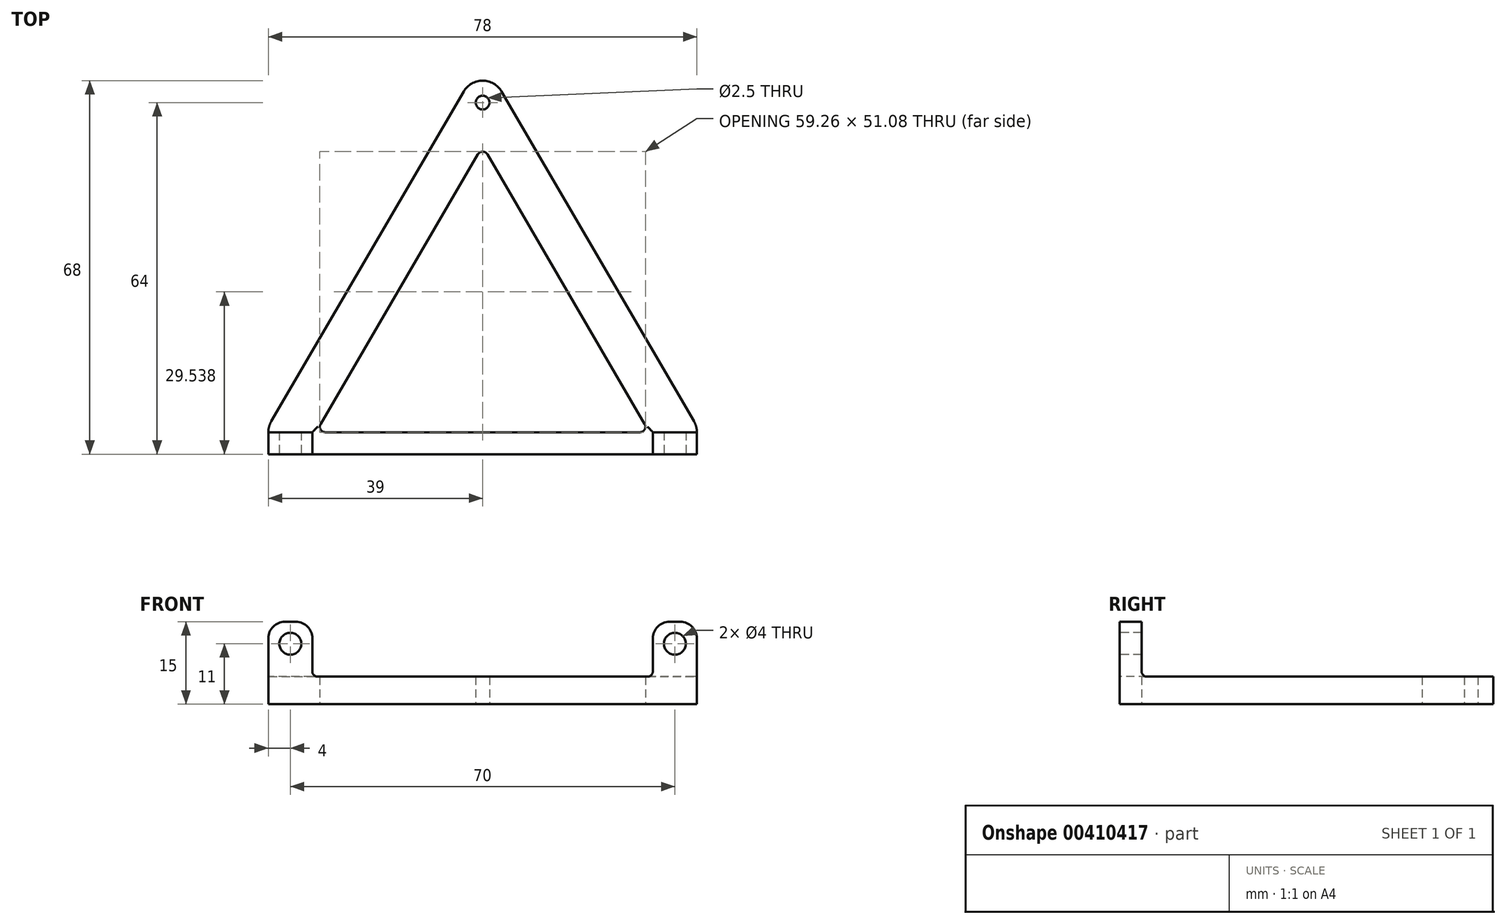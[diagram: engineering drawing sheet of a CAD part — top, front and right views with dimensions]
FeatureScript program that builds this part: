
annotation { "Feature Type Name" : "Feature", "Feature Type Description" : "" }
export const myFeature = defineFeature(function(context is Context, id is Id, definition is map)
    precondition{}
    {
        {
            var Q0;
            Q0=qCreatedBy(makeId("Top.planeOp"),FACE);
            var sketch = newSketch(context, id + "F0", { "sketchPlane" : qUnion([Q0])});
            skLineSegment(sketch, "E0", {"start": v(-35, 4) * mm, "end": v(35, 4) * mm, "construction": true});
            skLineSegment(sketch, "E1", {"start": v(35, 4) * mm, "end": v(0, 64) * mm, "construction": true});
            skLineSegment(sketch, "E2", {"start": v(0, 64) * mm, "end": v(-35, 4) * mm, "construction": true});
            skLineSegment(sketch, "E3.0", {"start": v(-3.46, 66.02) * mm, "end": v(-38.46, 6.02) * mm});
            skLineSegment(sketch, "E3.1", {"start": v(38.46, 6.02) * mm, "end": v(3.46, 66.02) * mm});
            skLineSegment(sketch, "E4.left", {"start": v(-39, 0) * mm, "end": v(-39, 4) * mm});
            skPoint(sketch, "E5", {"position": v(0, 4) * mm});
            skArc(sketch, "E6", {"start": v(-38.46, 6.02) * mm, "mid": v(-38.86, 5.04) * mm, "end": v(-39, 4) * mm});
            skLineSegment(sketch, "E7.0", {"start": v(-0.86, 54.58) * mm, "end": v(-29.5, 5.5) * mm});
            skLineSegment(sketch, "E7.1", {"start": v(29.5, 5.5) * mm, "end": v(0.86, 54.58) * mm});
            skLineSegment(sketch, "E8", {"start": v(-28.63, 4) * mm, "end": v(28.63, 4) * mm});
            skLineSegment(sketch, "E9", {"start": v(39, 4) * mm, "end": v(39, 0) * mm});
            skArc(sketch, "E10", {"start": v(38.46, 6.02) * mm, "mid": v(38.86, 5.04) * mm, "end": v(39, 4) * mm});
            skLineSegment(sketch, "E11", {"start": v(-39, 0) * mm, "end": v(39, 0) * mm});
            skPoint(sketch, "E12.visualSharp", {"position": v(0, 71.94) * mm});
            skArc(sketch, "E12.filletArc", {"start": v(3.46, 66.02) * mm, "mid": v(0, 68) * mm, "end": v(-3.46, 66.02) * mm});
            skPoint(sketch, "E13.visualSharp", {"position": v(0, 56.06) * mm});
            skArc(sketch, "E13.filletArc", {"start": v(0.86, 54.58) * mm, "mid": v(0, 55.08) * mm, "end": v(-0.86, 54.58) * mm});
            skPoint(sketch, "E14.visualSharp", {"position": v(-30.37, 4) * mm});
            skArc(sketch, "E14.filletArc", {"start": v(-29.5, 5.5) * mm, "mid": v(-29.5, 4.5) * mm, "end": v(-28.63, 4) * mm});
            skPoint(sketch, "E15.visualSharp", {"position": v(30.37, 4) * mm});
            skArc(sketch, "E15.filletArc", {"start": v(28.63, 4) * mm, "mid": v(29.5, 4.5) * mm, "end": v(29.5, 5.5) * mm});
            skCircle(sketch, "E16", {"center": v(0, 64) * mm, "radius": 1.25 * mm});
            skSolve(sketch);
        }
        {
            var Q0;
            Q0=makeQuery(id+"F0.imprint","IMPRINT",FACE,{"disambiguationData":[TD([[makeQuery(id+"F0.imprint","IMPRINT",EDGE,{"derivedFrom":sQuery(id+"F0.wireOp",EDGE,"E3.0")}),1.0]])]});
            extrude(context, id + "F1", {"entities" : qUnion([Q0]), "depth" : 5 * mm});
        }
        {
            var Q0;
            Q0=qCreatedBy(makeId("Front.planeOp"),FACE);
            var sketch = newSketch(context, id + "F2", { "sketchPlane" : qUnion([Q0])});
            skLineSegment(sketch, "E17.bottom", {"start": v(-39, 0) * mm, "end": v(-31, 0) * mm});
            skLineSegment(sketch, "E17.top", {"start": v(-36, 15) * mm, "end": v(-34, 15) * mm});
            skLineSegment(sketch, "E17.left", {"start": v(-39, 0) * mm, "end": v(-39, 12) * mm});
            skLineSegment(sketch, "E17.right", {"start": v(-31, 0) * mm, "end": v(-31, 12) * mm});
            skCircle(sketch, "E18", {"center": v(-35, 11) * mm, "radius": 2 * mm});
            skPoint(sketch, "E19.visualSharp", {"position": v(-31, 15) * mm});
            skArc(sketch, "E19.filletArc", {"start": v(-31, 12) * mm, "mid": v(-31.88, 14.12) * mm, "end": v(-34, 15) * mm});
            skPoint(sketch, "E20.visualSharp", {"position": v(-39, 15) * mm});
            skArc(sketch, "E20.filletArc", {"start": v(-36, 15) * mm, "mid": v(-38.12, 14.12) * mm, "end": v(-39, 12) * mm});
            skSolve(sketch);
        }
        {
            var Q0;
            Q0=makeQuery(id+"F2.imprint","IMPRINT",FACE,{"disambiguationData":[TD([[makeQuery(id+"F2.imprint","IMPRINT",EDGE,{"derivedFrom":sQuery(id+"F2.wireOp",EDGE,"E17.bottom")}),1.0]])]});
            extrude(context, id + "F3", {"entities" : qUnion([Q0]), "oppositeDirection" : true, "depth" : 4 * mm});
        }
        {
            var Q0;
            Q0=makeQuery(id+"F3.opExtrude","SWEPT_BODY",BODY,{"disambiguationData":[OSD([sQuery(id+"F2.wireOp",EDGE,"E17.bottom"),sQuery(id+"F2.wireOp",EDGE,"E17.top"),sQuery(id+"F2.wireOp",EDGE,"E17.left"),sQuery(id+"F2.wireOp",EDGE,"E17.right"),sQuery(id+"F2.wireOp",EDGE,"E18"),sQuery(id+"F2.wireOp",EDGE,"E19.filletArc"),sQuery(id+"F2.wireOp",EDGE,"E20.filletArc")])]});
            var Q1;
            Q1=qCreatedBy(makeId("Right.planeOp"),FACE);
            mirror(context, id + "F4", {"operationType" : NewBodyOperationType.ADD, "entities" : qUnion([Q0]), "mirrorPlane" : qUnion([Q1])});
        }
        {
            var Q0;
            Q0=makeQuery(id+"F4.boolean.opBoolean","INTERSECT",EDGE,{"derivedFrom":[makeQuery(id+"F1.opExtrude","CAP_FACE",FACE,{"disambiguationData":[OSD([sQuery(id+"F0.wireOp",EDGE,"E3.0"),sQuery(id+"F0.wireOp",EDGE,"E3.1"),sQuery(id+"F0.wireOp",EDGE,"E4.left"),sQuery(id+"F0.wireOp",EDGE,"E6"),sQuery(id+"F0.wireOp",EDGE,"E7.0"),sQuery(id+"F0.wireOp",EDGE,"E7.1"),sQuery(id+"F0.wireOp",EDGE,"E8"),sQuery(id+"F0.wireOp",EDGE,"E9"),sQuery(id+"F0.wireOp",EDGE,"E10"),sQuery(id+"F0.wireOp",EDGE,"E11"),sQuery(id+"F0.wireOp",EDGE,"E12.filletArc"),sQuery(id+"F0.wireOp",EDGE,"E13.filletArc"),sQuery(id+"F0.wireOp",EDGE,"E14.filletArc"),sQuery(id+"F0.wireOp",EDGE,"E15.filletArc"),sQuery(id+"F0.wireOp",EDGE,"E16")])],"isStart":false}),makeQuery(id+"F3.opExtrude","CAP_FACE",FACE,{"disambiguationData":[OSD([sQuery(id+"F2.wireOp",EDGE,"E17.bottom"),sQuery(id+"F2.wireOp",EDGE,"E17.top"),sQuery(id+"F2.wireOp",EDGE,"E17.left"),sQuery(id+"F2.wireOp",EDGE,"E17.right"),sQuery(id+"F2.wireOp",EDGE,"E18"),sQuery(id+"F2.wireOp",EDGE,"E19.filletArc"),sQuery(id+"F2.wireOp",EDGE,"E20.filletArc")])],"isStart":false})]});
            var Q1;
            Q1=makeQuery(id+"F4.boolean.opBoolean","INTERSECT",EDGE,{"derivedFrom":[makeQuery(id+"F1.opExtrude","CAP_FACE",FACE,{"disambiguationData":[OSD([sQuery(id+"F0.wireOp",EDGE,"E3.0"),sQuery(id+"F0.wireOp",EDGE,"E3.1"),sQuery(id+"F0.wireOp",EDGE,"E4.left"),sQuery(id+"F0.wireOp",EDGE,"E6"),sQuery(id+"F0.wireOp",EDGE,"E7.0"),sQuery(id+"F0.wireOp",EDGE,"E7.1"),sQuery(id+"F0.wireOp",EDGE,"E8"),sQuery(id+"F0.wireOp",EDGE,"E9"),sQuery(id+"F0.wireOp",EDGE,"E10"),sQuery(id+"F0.wireOp",EDGE,"E11"),sQuery(id+"F0.wireOp",EDGE,"E12.filletArc"),sQuery(id+"F0.wireOp",EDGE,"E13.filletArc"),sQuery(id+"F0.wireOp",EDGE,"E14.filletArc"),sQuery(id+"F0.wireOp",EDGE,"E15.filletArc"),sQuery(id+"F0.wireOp",EDGE,"E16")])],"isStart":false}),makeQuery(id+"F3.opExtrude","SWEPT_FACE",FACE,{"disambiguationData":[OSD([sQuery(id+"F2.wireOp",EDGE,"E17.right")])]})]});
            var Q2;
            Q2=makeQuery(id+"F4.boolean.opBoolean","INTERSECT",EDGE,{"derivedFrom":[makeQuery(id+"F1.opExtrude","CAP_FACE",FACE,{"disambiguationData":[OSD([sQuery(id+"F0.wireOp",EDGE,"E3.0"),sQuery(id+"F0.wireOp",EDGE,"E3.1"),sQuery(id+"F0.wireOp",EDGE,"E4.left"),sQuery(id+"F0.wireOp",EDGE,"E6"),sQuery(id+"F0.wireOp",EDGE,"E7.0"),sQuery(id+"F0.wireOp",EDGE,"E7.1"),sQuery(id+"F0.wireOp",EDGE,"E8"),sQuery(id+"F0.wireOp",EDGE,"E9"),sQuery(id+"F0.wireOp",EDGE,"E10"),sQuery(id+"F0.wireOp",EDGE,"E11"),sQuery(id+"F0.wireOp",EDGE,"E12.filletArc"),sQuery(id+"F0.wireOp",EDGE,"E13.filletArc"),sQuery(id+"F0.wireOp",EDGE,"E14.filletArc"),sQuery(id+"F0.wireOp",EDGE,"E15.filletArc"),sQuery(id+"F0.wireOp",EDGE,"E16")])],"isStart":false}),makeQuery(id+"F4.opPattern","COPY",FACE,{"derivedFrom":makeQuery(id+"F3.opExtrude","SWEPT_FACE",FACE,{"disambiguationData":[OSD([sQuery(id+"F2.wireOp",EDGE,"E17.right")])]}),"instanceName":"1"})]});
            var Q3;
            Q3=makeQuery(id+"F4.boolean.opBoolean","INTERSECT",EDGE,{"derivedFrom":[makeQuery(id+"F1.opExtrude","CAP_FACE",FACE,{"disambiguationData":[OSD([sQuery(id+"F0.wireOp",EDGE,"E3.0"),sQuery(id+"F0.wireOp",EDGE,"E3.1"),sQuery(id+"F0.wireOp",EDGE,"E4.left"),sQuery(id+"F0.wireOp",EDGE,"E6"),sQuery(id+"F0.wireOp",EDGE,"E7.0"),sQuery(id+"F0.wireOp",EDGE,"E7.1"),sQuery(id+"F0.wireOp",EDGE,"E8"),sQuery(id+"F0.wireOp",EDGE,"E9"),sQuery(id+"F0.wireOp",EDGE,"E10"),sQuery(id+"F0.wireOp",EDGE,"E11"),sQuery(id+"F0.wireOp",EDGE,"E12.filletArc"),sQuery(id+"F0.wireOp",EDGE,"E13.filletArc"),sQuery(id+"F0.wireOp",EDGE,"E14.filletArc"),sQuery(id+"F0.wireOp",EDGE,"E15.filletArc"),sQuery(id+"F0.wireOp",EDGE,"E16")])],"isStart":false}),makeQuery(id+"F4.opPattern","COPY",FACE,{"derivedFrom":makeQuery(id+"F3.opExtrude","CAP_FACE",FACE,{"disambiguationData":[OSD([sQuery(id+"F2.wireOp",EDGE,"E17.bottom"),sQuery(id+"F2.wireOp",EDGE,"E17.top"),sQuery(id+"F2.wireOp",EDGE,"E17.left"),sQuery(id+"F2.wireOp",EDGE,"E17.right"),sQuery(id+"F2.wireOp",EDGE,"E18"),sQuery(id+"F2.wireOp",EDGE,"E19.filletArc"),sQuery(id+"F2.wireOp",EDGE,"E20.filletArc")])],"isStart":false}),"instanceName":"1"})]});
            fillet(context, id + "F5", {"entities" : qUnion([Q0, Q1, Q2, Q3]), "radius" : 1 * mm, "tangentPropagation" : true, "allowEdgeOverflow" : false});
        }
    });
